# Revit family: Shower-Shower_Door-KOHLER-ODEON-K-17117T_1
name_source: partatom
category: Specialty Equipment
revit_build: Autodesk Revit 2017 (Build: 20160225_1515(x64)
units: mm (PartAtom-declared; Revit-internal decimal feet)

## family parameters
Cut with Voids When Loaded = No
Host = Face
OmniClass Number = 23.31.17.17
OmniClass Title = Shower Enclosures
Part Type = Normal
Room Calculation Point = No
Round Connector Dimension = Use Diameter
Shared = No

## types (2) — shared parameters
ADA Compliant = No
Assembly Code = C1030200
Date Modified = 09/24/2021
Default Elevation = 0"
Description = HINGED, L SHAPE, SEALED, 8
Height = 72 13/16"
Length = 31 9/16"
Manufacturer = KOHLER Co.
Master Format 2014 = 10 28 19.16
Master Format 2014 Name = Shower Doors
Material = Aluminum
Product Name = ODEON
URL = http://www.kohler.com.cn
WaterSense Certified = No
Width = 31 1/2"

## per-type parameters (varying)
| type | Finish | Model | Type |
| SH-Bright Silver | Kohler-Metal-SH-Bright_Silver | K-17117T-L-SH | 1 |
| 0-White | Kohler-Metal-0-White | K-17117T-L-0 | 2 |

## geometry (parser evidence)
native form markers: Sweep x6
no freeform markers — native parametric forms only
